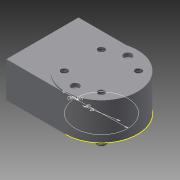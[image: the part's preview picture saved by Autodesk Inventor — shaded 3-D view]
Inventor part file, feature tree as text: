
AUTODESK INVENTOR PART (.ipt)
format: ipt  version: 2013 (Build 170138000, 138)  size: 153,600 bytes
history: native  units: mm
features: chamfer x5, extrude x4, thread x4, sketch x3, hole x3
ambient origin geometry x8: Origin, YZ Plane, XZ Plane, XY Plane, X Axis, Y Axis, Z Axis, Center Point
bodies: Solid1 (feature_tree)
feature tree (19):
  sketch  "Sketch1"  dims[d0=55.0mm d13=28.0mm d14=0.0mm]
  extrude  "Extrusion1"  Depth=28.0mm TaperAngle=0.0deg
  extrude  "Extrusion2"  Depth=55.0mm
  hole  "Hole1"  [1 undecoded]
  hole  "Hole2"  [1 undecoded]
  sketch  "Sketch3"  dims[d17=27.0mm d18=0.0mm d19=20.0mm d20=80.0mm d22=360.0deg d24=6.0mm d25=6.0mm d26=14.55mm d27=4.15mm d28=90.0deg d29=3.0mm d30=20.594885mm d31=4.917mm d32=6.0mm d33=14.55mm d34=4.15mm d35=90.0deg d36=8.0mm d37=20.594885mm d38=25.0mm d39=3.0mm d40=0.0mm d41=0.5mm d42=2.0mm d43=45.0deg d44=40.0mm d45=6.0mm d46=80.0mm d48=360.0deg d50=6.0mm d51=0.0mm d52=10.0mm d53=0.0mm d54=10.0mm d55=0.0mm d56=10.0mm d57=0.0mm d58=10.0mm d59=0.0mm d60=0.5mm d61=2.0mm d62=45.0deg d63=0.5mm d64=2.0mm d65=45.0deg d66=0.5mm d67=2.0mm d68=45.0deg d69=0.5mm d70=2.0mm d71=45.0deg d72=6.0mm d73=6.0mm d74=14.55mm d75=4.15mm d76=90.0deg d77=3.0mm d78=20.594885mm]
  extrude  "Extrusion3"  Depth=25.0mm
  chamfer  "Chamfer1"  Distance=3.0mm
  extrude  "Extrusion4"  Depth=0.5mm TaperAngle=45.0deg
  thread  "Thread1"  [1 undecoded]
  thread  "Thread2"  [1 undecoded]
  thread  "Thread3"  [1 undecoded]
  thread  "Thread4"  [1 undecoded]
  chamfer  "Chamfer2"  Distance=10.0mm
  chamfer  "Chamfer3"  Distance=10.0mm
  chamfer  "Chamfer4"  Distance=10.0mm
  chamfer  "Chamfer5"  Distance=10.0mm
  hole  "Hole3"  [1 undecoded]
  sketch  "Sketch2"  dims[d15=45.0mm d16=55.0mm]
note: 7 required parameter values undecoded (feature->parameter linkage not recoverable at this tier; creation-order binding heuristic only, values carry confidence <= 0.55)
